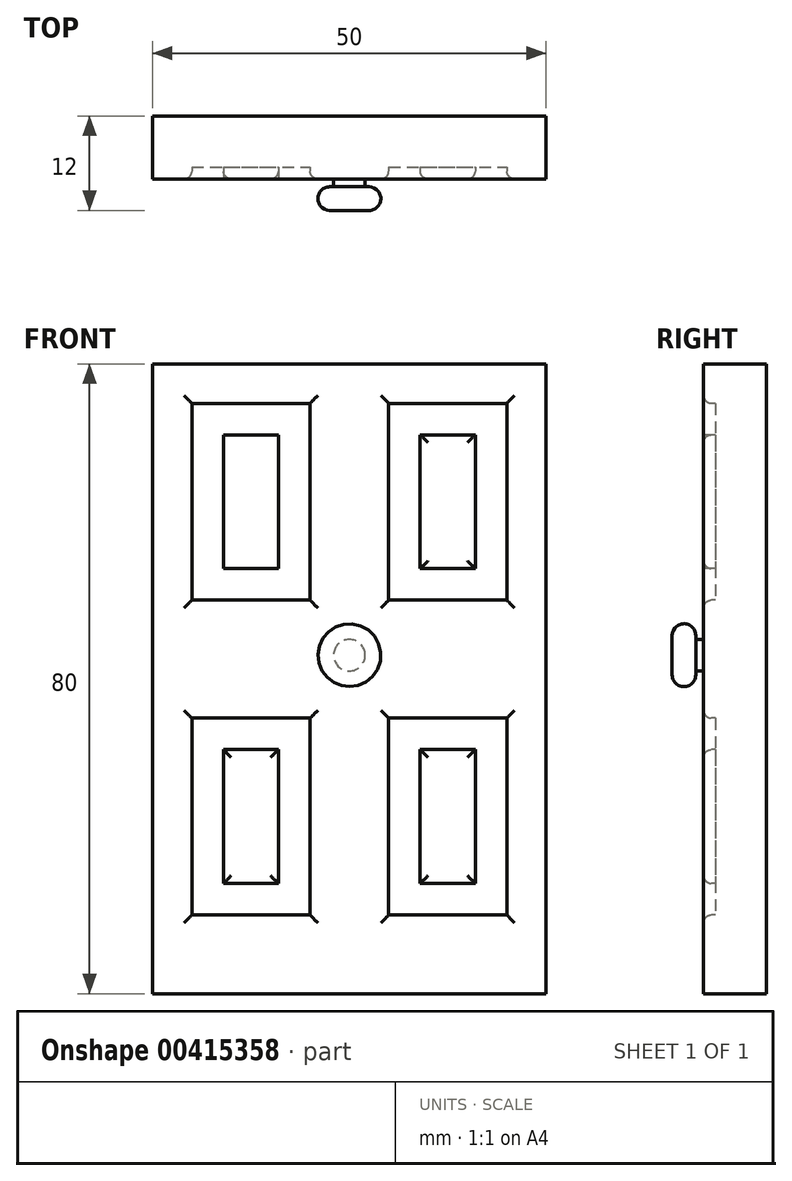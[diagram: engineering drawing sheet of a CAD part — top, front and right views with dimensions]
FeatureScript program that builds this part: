
annotation { "Feature Type Name" : "Feature", "Feature Type Description" : "" }
export const myFeature = defineFeature(function(context is Context, id is Id, definition is map)
    precondition{}
    {
        {
            var Q0;
            Q0=qCreatedBy(makeId("Front.planeOp"),FACE);
            var sketch = newSketch(context, id + "F0", { "sketchPlane" : qUnion([Q0])});
            skLineSegment(sketch, "E0.bottom", {"start": v(0, 0) * mm, "end": v(50, 0) * mm});
            skLineSegment(sketch, "E0.top", {"start": v(0, 80) * mm, "end": v(50, 80) * mm});
            skLineSegment(sketch, "E0.left", {"start": v(0, 0) * mm, "end": v(0, 80) * mm});
            skLineSegment(sketch, "E0.right", {"start": v(50, 0) * mm, "end": v(50, 80) * mm});
            skSolve(sketch);
        }
        {
            var Q0;
            Q0=makeQuery(id+"F0.imprint","IMPRINT",FACE,{"disambiguationData":[TD([[makeQuery(id+"F0.imprint","IMPRINT",EDGE,{"derivedFrom":sQuery(id+"F0.wireOp",EDGE,"E0.bottom")}),1.0]])]});
            extrude(context, id + "F1", {"entities" : qUnion([Q0]), "depth" : 8 * mm});
        }
        {
            var Q0;
            Q0=makeQuery(id+"F1.opExtrude","CAP_FACE",FACE,{"disambiguationData":[OSD([sQuery(id+"F0.wireOp",EDGE,"E0.bottom"),sQuery(id+"F0.wireOp",EDGE,"E0.top"),sQuery(id+"F0.wireOp",EDGE,"E0.left"),sQuery(id+"F0.wireOp",EDGE,"E0.right")])],"isStart":false});
            var sketch = newSketch(context, id + "F2", { "sketchPlane" : qUnion([Q0])});
            skLineSegment(sketch, "E1.bottom", {"start": v(5, 75) * mm, "end": v(20, 75) * mm});
            skLineSegment(sketch, "E1.top", {"start": v(5, 50) * mm, "end": v(20, 50) * mm});
            skLineSegment(sketch, "E1.left", {"start": v(5, 75) * mm, "end": v(5, 50) * mm});
            skLineSegment(sketch, "E1.right", {"start": v(20, 75) * mm, "end": v(20, 50) * mm});
            skLineSegment(sketch, "E2.bottom", {"start": v(9, 71) * mm, "end": v(16, 71) * mm});
            skLineSegment(sketch, "E2.top", {"start": v(9, 54) * mm, "end": v(16, 54) * mm});
            skLineSegment(sketch, "E2.left", {"start": v(9, 71) * mm, "end": v(9, 54) * mm});
            skLineSegment(sketch, "E2.right", {"start": v(16, 71) * mm, "end": v(16, 54) * mm});
            skLineSegment(sketch, "E3.0.1.0", {"start": v(5, 35) * mm, "end": v(20, 35) * mm});
            skLineSegment(sketch, "E3.0.1.1", {"start": v(9, 31) * mm, "end": v(16, 31) * mm});
            skLineSegment(sketch, "E3.0.1.2", {"start": v(20, 35) * mm, "end": v(20, 10) * mm});
            skLineSegment(sketch, "E3.0.1.3", {"start": v(16, 31) * mm, "end": v(16, 14) * mm});
            skLineSegment(sketch, "E3.0.1.4", {"start": v(5, 35) * mm, "end": v(5, 10) * mm});
            skLineSegment(sketch, "E3.0.1.5", {"start": v(9, 31) * mm, "end": v(9, 14) * mm});
            skLineSegment(sketch, "E3.0.1.6", {"start": v(9, 14) * mm, "end": v(16, 14) * mm});
            skLineSegment(sketch, "E3.0.1.7", {"start": v(5, 10) * mm, "end": v(20, 10) * mm});
            skLineSegment(sketch, "E3.1.0.0", {"start": v(30, 75) * mm, "end": v(45, 75) * mm});
            skLineSegment(sketch, "E3.1.0.1", {"start": v(34, 71) * mm, "end": v(41, 71) * mm});
            skLineSegment(sketch, "E3.1.0.2", {"start": v(45, 75) * mm, "end": v(45, 50) * mm});
            skLineSegment(sketch, "E3.1.0.3", {"start": v(41, 71) * mm, "end": v(41, 54) * mm});
            skLineSegment(sketch, "E3.1.0.4", {"start": v(30, 75) * mm, "end": v(30, 50) * mm});
            skLineSegment(sketch, "E3.1.0.5", {"start": v(34, 71) * mm, "end": v(34, 54) * mm});
            skLineSegment(sketch, "E3.1.0.6", {"start": v(34, 54) * mm, "end": v(41, 54) * mm});
            skLineSegment(sketch, "E3.1.0.7", {"start": v(30, 50) * mm, "end": v(45, 50) * mm});
            skLineSegment(sketch, "E3.1.1.0", {"start": v(30, 35) * mm, "end": v(45, 35) * mm});
            skLineSegment(sketch, "E3.1.1.1", {"start": v(34, 31) * mm, "end": v(41, 31) * mm});
            skLineSegment(sketch, "E3.1.1.2", {"start": v(45, 35) * mm, "end": v(45, 10) * mm});
            skLineSegment(sketch, "E3.1.1.3", {"start": v(41, 31) * mm, "end": v(41, 14) * mm});
            skLineSegment(sketch, "E3.1.1.4", {"start": v(30, 35) * mm, "end": v(30, 10) * mm});
            skLineSegment(sketch, "E3.1.1.5", {"start": v(34, 31) * mm, "end": v(34, 14) * mm});
            skLineSegment(sketch, "E3.1.1.6", {"start": v(34, 14) * mm, "end": v(41, 14) * mm});
            skLineSegment(sketch, "E3.1.1.7", {"start": v(30, 10) * mm, "end": v(45, 10) * mm});
            skLineSegment(sketch, "E3.direction1", {"start": v(5, 50) * mm, "end": v(30, 50) * mm, "construction": true});
            skLineSegment(sketch, "E3.direction2", {"start": v(5, 50) * mm, "end": v(5, 10) * mm, "construction": true});
            skSolve(sketch);
        }
        {
            var Q0;
            Q0=makeQuery(id+"F2.imprint","IMPRINT",FACE,{"disambiguationData":[TD([[makeQuery(id+"F2.imprint","IMPRINT",EDGE,{"derivedFrom":sQuery(id+"F2.wireOp",EDGE,"E1.bottom")}),-1.0]])]});
            var Q1;
            Q1=makeQuery(id+"F2.imprint","IMPRINT",FACE,{"disambiguationData":[TD([[makeQuery(id+"F2.imprint","IMPRINT",EDGE,{"derivedFrom":sQuery(id+"F2.wireOp",EDGE,"E3.1.0.0")}),-1.0]])]});
            var Q2;
            Q2=makeQuery(id+"F2.imprint","IMPRINT",FACE,{"disambiguationData":[TD([[makeQuery(id+"F2.imprint","IMPRINT",EDGE,{"derivedFrom":sQuery(id+"F2.wireOp",EDGE,"E3.0.1.0")}),-1.0]])]});
            var Q3;
            Q3=makeQuery(id+"F2.imprint","IMPRINT",FACE,{"disambiguationData":[TD([[makeQuery(id+"F2.imprint","IMPRINT",EDGE,{"derivedFrom":sQuery(id+"F2.wireOp",EDGE,"E3.1.1.0")}),-1.0]])]});
            extrude(context, id + "F3", {"entities" : qUnion([Q0, Q1, Q2, Q3]), "operationType" : NewBodyOperationType.REMOVE, "oppositeDirection" : true, "depth" : 1.5 * mm});
        }
        {
            var Q0;
            Q0=makeQuery(id+"F3.boolean.opBoolean","COPY",EDGE,{"derivedFrom":makeQuery(id+"F3.opExtrude","CAP_EDGE",EDGE,{"disambiguationData":[OSD([sQuery(id+"F2.wireOp",EDGE,"E2.right")])],"isStart":true})});
            var Q1;
            Q1=makeQuery(id+"F3.boolean.opBoolean","COPY",EDGE,{"derivedFrom":makeQuery(id+"F3.opExtrude","CAP_EDGE",EDGE,{"disambiguationData":[OSD([sQuery(id+"F2.wireOp",EDGE,"E2.bottom")])],"isStart":true})});
            var Q2;
            Q2=makeQuery(id+"F3.boolean.opBoolean","COPY",EDGE,{"derivedFrom":makeQuery(id+"F3.opExtrude","CAP_EDGE",EDGE,{"disambiguationData":[OSD([sQuery(id+"F2.wireOp",EDGE,"E2.left")])],"isStart":true})});
            var Q3;
            Q3=makeQuery(id+"F3.boolean.opBoolean","COPY",EDGE,{"derivedFrom":makeQuery(id+"F3.opExtrude","CAP_EDGE",EDGE,{"disambiguationData":[OSD([sQuery(id+"F2.wireOp",EDGE,"E2.top")])],"isStart":true})});
            var Q4;
            Q4=makeQuery(id+"F3.boolean.opBoolean","COPY",EDGE,{"derivedFrom":makeQuery(id+"F3.opExtrude","CAP_EDGE",EDGE,{"disambiguationData":[OSD([sQuery(id+"F2.wireOp",EDGE,"E1.left")])],"isStart":true})});
            var Q5;
            Q5=makeQuery(id+"F3.boolean.opBoolean","COPY",EDGE,{"derivedFrom":makeQuery(id+"F3.opExtrude","CAP_EDGE",EDGE,{"disambiguationData":[OSD([sQuery(id+"F2.wireOp",EDGE,"E1.bottom")])],"isStart":true})});
            var Q6;
            Q6=makeQuery(id+"F3.boolean.opBoolean","COPY",EDGE,{"derivedFrom":makeQuery(id+"F3.opExtrude","CAP_EDGE",EDGE,{"disambiguationData":[OSD([sQuery(id+"F2.wireOp",EDGE,"E1.right")])],"isStart":true})});
            var Q7;
            Q7=makeQuery(id+"F3.boolean.opBoolean","COPY",EDGE,{"derivedFrom":makeQuery(id+"F3.opExtrude","CAP_EDGE",EDGE,{"disambiguationData":[OSD([sQuery(id+"F2.wireOp",EDGE,"E1.top")])],"isStart":true})});
            var Q8;
            Q8=makeQuery(id+"F3.boolean.opBoolean","COPY",EDGE,{"derivedFrom":makeQuery(id+"F3.opExtrude","CAP_EDGE",EDGE,{"disambiguationData":[OSD([sQuery(id+"F2.wireOp",EDGE,"E3.1.0.0")])],"isStart":true})});
            var Q9;
            Q9=makeQuery(id+"F3.boolean.opBoolean","COPY",EDGE,{"derivedFrom":makeQuery(id+"F3.opExtrude","CAP_EDGE",EDGE,{"disambiguationData":[OSD([sQuery(id+"F2.wireOp",EDGE,"E3.1.0.2")])],"isStart":true})});
            var Q10;
            Q10=makeQuery(id+"F3.boolean.opBoolean","COPY",EDGE,{"derivedFrom":makeQuery(id+"F3.opExtrude","CAP_EDGE",EDGE,{"disambiguationData":[OSD([sQuery(id+"F2.wireOp",EDGE,"E3.1.0.1")])],"isStart":true})});
            var Q11;
            Q11=makeQuery(id+"F3.boolean.opBoolean","COPY",EDGE,{"derivedFrom":makeQuery(id+"F3.opExtrude","CAP_EDGE",EDGE,{"disambiguationData":[OSD([sQuery(id+"F2.wireOp",EDGE,"E3.1.0.4")])],"isStart":true})});
            var Q12;
            Q12=makeQuery(id+"F3.boolean.opBoolean","COPY",EDGE,{"derivedFrom":makeQuery(id+"F3.opExtrude","CAP_EDGE",EDGE,{"disambiguationData":[OSD([sQuery(id+"F2.wireOp",EDGE,"E3.1.0.5")])],"isStart":true})});
            var Q13;
            Q13=makeQuery(id+"F3.boolean.opBoolean","COPY",EDGE,{"derivedFrom":makeQuery(id+"F3.opExtrude","CAP_EDGE",EDGE,{"disambiguationData":[OSD([sQuery(id+"F2.wireOp",EDGE,"E3.1.0.3")])],"isStart":true})});
            var Q14;
            Q14=makeQuery(id+"F3.boolean.opBoolean","COPY",EDGE,{"derivedFrom":makeQuery(id+"F3.opExtrude","CAP_EDGE",EDGE,{"disambiguationData":[OSD([sQuery(id+"F2.wireOp",EDGE,"E3.1.0.6")])],"isStart":true})});
            var Q15;
            Q15=makeQuery(id+"F3.boolean.opBoolean","COPY",EDGE,{"derivedFrom":makeQuery(id+"F3.opExtrude","CAP_EDGE",EDGE,{"disambiguationData":[OSD([sQuery(id+"F2.wireOp",EDGE,"E3.1.0.7")])],"isStart":true})});
            var Q16;
            Q16=makeQuery(id+"F3.boolean.opBoolean","COPY",EDGE,{"derivedFrom":makeQuery(id+"F3.opExtrude","CAP_EDGE",EDGE,{"disambiguationData":[OSD([sQuery(id+"F2.wireOp",EDGE,"E3.1.1.0")])],"isStart":true})});
            var Q17;
            Q17=makeQuery(id+"F3.boolean.opBoolean","COPY",EDGE,{"derivedFrom":makeQuery(id+"F3.opExtrude","CAP_EDGE",EDGE,{"disambiguationData":[OSD([sQuery(id+"F2.wireOp",EDGE,"E3.1.1.1")])],"isStart":true})});
            var Q18;
            Q18=makeQuery(id+"F3.boolean.opBoolean","COPY",EDGE,{"derivedFrom":makeQuery(id+"F3.opExtrude","CAP_EDGE",EDGE,{"disambiguationData":[OSD([sQuery(id+"F2.wireOp",EDGE,"E3.1.1.5")])],"isStart":true})});
            var Q19;
            Q19=makeQuery(id+"F3.boolean.opBoolean","COPY",EDGE,{"derivedFrom":makeQuery(id+"F3.opExtrude","CAP_EDGE",EDGE,{"disambiguationData":[OSD([sQuery(id+"F2.wireOp",EDGE,"E3.1.1.6")])],"isStart":true})});
            var Q20;
            Q20=makeQuery(id+"F3.boolean.opBoolean","COPY",EDGE,{"derivedFrom":makeQuery(id+"F3.opExtrude","CAP_EDGE",EDGE,{"disambiguationData":[OSD([sQuery(id+"F2.wireOp",EDGE,"E3.1.1.3")])],"isStart":true})});
            var Q21;
            Q21=makeQuery(id+"F3.boolean.opBoolean","COPY",EDGE,{"derivedFrom":makeQuery(id+"F3.opExtrude","CAP_EDGE",EDGE,{"disambiguationData":[OSD([sQuery(id+"F2.wireOp",EDGE,"E3.1.1.2")])],"isStart":true})});
            var Q22;
            Q22=makeQuery(id+"F3.boolean.opBoolean","COPY",EDGE,{"derivedFrom":makeQuery(id+"F3.opExtrude","CAP_EDGE",EDGE,{"disambiguationData":[OSD([sQuery(id+"F2.wireOp",EDGE,"E3.1.1.7")])],"isStart":true})});
            var Q23;
            Q23=makeQuery(id+"F3.boolean.opBoolean","COPY",EDGE,{"derivedFrom":makeQuery(id+"F3.opExtrude","CAP_EDGE",EDGE,{"disambiguationData":[OSD([sQuery(id+"F2.wireOp",EDGE,"E3.1.1.4")])],"isStart":true})});
            var Q24;
            Q24=makeQuery(id+"F3.boolean.opBoolean","COPY",EDGE,{"derivedFrom":makeQuery(id+"F3.opExtrude","CAP_EDGE",EDGE,{"disambiguationData":[OSD([sQuery(id+"F2.wireOp",EDGE,"E3.0.1.2")])],"isStart":true})});
            var Q25;
            Q25=makeQuery(id+"F3.boolean.opBoolean","COPY",EDGE,{"derivedFrom":makeQuery(id+"F3.opExtrude","CAP_EDGE",EDGE,{"disambiguationData":[OSD([sQuery(id+"F2.wireOp",EDGE,"E3.0.1.3")])],"isStart":true})});
            var Q26;
            Q26=makeQuery(id+"F3.boolean.opBoolean","COPY",EDGE,{"derivedFrom":makeQuery(id+"F3.opExtrude","CAP_EDGE",EDGE,{"disambiguationData":[OSD([sQuery(id+"F2.wireOp",EDGE,"E3.0.1.5")])],"isStart":true})});
            var Q27;
            Q27=makeQuery(id+"F3.boolean.opBoolean","COPY",EDGE,{"derivedFrom":makeQuery(id+"F3.opExtrude","CAP_EDGE",EDGE,{"disambiguationData":[OSD([sQuery(id+"F2.wireOp",EDGE,"E3.0.1.4")])],"isStart":true})});
            var Q28;
            Q28=makeQuery(id+"F3.boolean.opBoolean","COPY",EDGE,{"derivedFrom":makeQuery(id+"F3.opExtrude","CAP_EDGE",EDGE,{"disambiguationData":[OSD([sQuery(id+"F2.wireOp",EDGE,"E3.0.1.0")])],"isStart":true})});
            var Q29;
            Q29=makeQuery(id+"F3.boolean.opBoolean","COPY",EDGE,{"derivedFrom":makeQuery(id+"F3.opExtrude","CAP_EDGE",EDGE,{"disambiguationData":[OSD([sQuery(id+"F2.wireOp",EDGE,"E3.0.1.1")])],"isStart":true})});
            var Q30;
            Q30=makeQuery(id+"F3.boolean.opBoolean","COPY",EDGE,{"derivedFrom":makeQuery(id+"F3.opExtrude","CAP_EDGE",EDGE,{"disambiguationData":[OSD([sQuery(id+"F2.wireOp",EDGE,"E3.0.1.6")])],"isStart":true})});
            var Q31;
            Q31=makeQuery(id+"F3.boolean.opBoolean","COPY",EDGE,{"derivedFrom":makeQuery(id+"F3.opExtrude","CAP_EDGE",EDGE,{"disambiguationData":[OSD([sQuery(id+"F2.wireOp",EDGE,"E3.0.1.7")])],"isStart":true})});
            fillet(context, id + "F4", {"entities" : qUnion([Q0, Q1, Q2, Q3, Q4, Q5, Q6, Q7, Q8, Q9, Q10, Q11, Q12, Q13, Q14, Q15, Q16, Q17, Q18, Q19, Q20, Q21, Q22, Q23, Q24, Q25, Q26, Q27, Q28, Q29, Q30, Q31]), "radius" : 1 * mm, "tangentPropagation" : true, "allowEdgeOverflow" : false});
        }
        {
            var Q0;
            {var subQ0=sQuery(id+"F0.wireOp",EDGE,"E0.left");var subQ1=sQuery(id+"F0.wireOp",EDGE,"E0.bottom");var subQ2=sQuery(id+"F0.wireOp",EDGE,"E0.right");var subQ3=sQuery(id+"F0.wireOp",EDGE,"E0.top");Q0=makeQuery(id+"F3.boolean.opBoolean","SPLIT",FACE,{"disambiguationData":[TD([makeQuery(id+"F1.opExtrude","SWEPT_FACE",FACE,{"disambiguationData":[OSD([subQ1])]})])],"derivedFrom":makeQuery(id+"F1.opExtrude","CAP_FACE",FACE,{"disambiguationData":[OSD([subQ1,subQ3,subQ0,subQ2])],"isStart":false})});}
            var sketch = newSketch(context, id + "F5", { "sketchPlane" : qUnion([Q0])});
            skCircle(sketch, "E4", {"center": v(25, 43) * mm, "radius": 2 * mm});
            skSolve(sketch);
        }
        {
            var Q0;
            Q0=makeQuery(id+"F5.imprint","IMPRINT",FACE,{"disambiguationData":[TD([[makeQuery(id+"F5.imprint","IMPRINT",EDGE,{"derivedFrom":sQuery(id+"F5.wireOp",EDGE,"E4")}),1.0]])]});
            extrude(context, id + "F6", {"entities" : qUnion([Q0]), "operationType" : NewBodyOperationType.ADD, "depth" : 1 * mm});
        }
        {
            var Q0;
            Q0=makeQuery(id+"F6.opExtrude","CAP_FACE",FACE,{"disambiguationData":[OSD([sQuery(id+"F5.wireOp",EDGE,"E4")])],"isStart":false});
            var sketch = newSketch(context, id + "F7", { "sketchPlane" : qUnion([Q0])});
            skCircle(sketch, "E5", {"center": v(25, 43) * mm, "radius": 4 * mm});
            skSolve(sketch);
        }
        {
            var Q0;
            Q0=makeQuery(id+"F7.imprint","IMPRINT",FACE,{"disambiguationData":[TD([[makeQuery(id+"F7.imprint","IMPRINT",EDGE,{"derivedFrom":makeQuery(id+"F6.opExtrude","CAP_EDGE",EDGE,{"disambiguationData":[OSD([sQuery(id+"F5.wireOp",EDGE,"E4")])],"isStart":false})}),1.0]])]});
            var Q1;
            Q1=makeQuery(id+"F7.imprint","IMPRINT",FACE,{"disambiguationData":[TD([[makeQuery(id+"F7.imprint","IMPRINT",EDGE,{"derivedFrom":sQuery(id+"F7.wireOp",EDGE,"E5")}),1.0]])]});
            extrude(context, id + "F8", {"entities" : qUnion([Q0, Q1]), "operationType" : NewBodyOperationType.ADD, "depth" : 3 * mm});
        }
        {
            var Q0;
            Q0=makeQuery(id+"F8.opExtrude","CAP_EDGE",EDGE,{"disambiguationData":[OSD([sQuery(id+"F7.wireOp",EDGE,"E5")])],"isStart":false});
            var Q1;
            Q1=makeQuery(id+"F8.opExtrude","CAP_EDGE",EDGE,{"disambiguationData":[OSD([sQuery(id+"F7.wireOp",EDGE,"E5")])],"isStart":true});
            fillet(context, id + "F9", {"entities" : qUnion([Q0, Q1]), "radius" : 1.5 * mm, "tangentPropagation" : true, "allowEdgeOverflow" : false});
        }
    });
